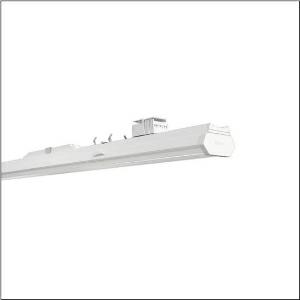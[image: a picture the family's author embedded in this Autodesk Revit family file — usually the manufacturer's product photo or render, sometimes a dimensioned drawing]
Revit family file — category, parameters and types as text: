
# Revit family: licross_r__11_protected_mo_51ts12vn465fd_14fd
name_source: partatom
category: Lighting Fixtures
units: mm (PartAtom-declared; Revit-internal decimal feet)

## family parameters
Cut with Voids When Loaded = No
Host = Face
Light Source = No
Part Type = Normal
Room Calculation Point = No
Round Connector Dimension = Use Diameter
Shared = No

## types (1)
- --- (1 x LED, 1000 lm, 8 W, 4000K)
    Apparent Load = 8 VA
    CIE Flux Codes = 54 82 95 97 100
    Color Rendering = 80
    Color Temperature = 4000K
    Default Elevation = 1800 mm
    Description = Licross® 11 Protected MO, luminaire insert, of sheet steel, galvanised, coil coated, white, length: 1.500mm, width: 90mm, height: 101mm, LED rated luminous flux: 6.530lm, light colour: 840, control gear: DALI 2, CLO, control gear: ECG DALI, with plug, 6-pole, with phase selection, mains connection: 220..240V, AC/DC, 0/50..60Hz, halogen-free wiring, for central battery installations according to DIN EN 60598-2-22, for emergency light function, without changeover relay, primary optical cover: cover, of PMMA, light emission: direct with ceiling illumination distribution, protection rating (complete): IP50, insulation class (complete): insulation class I (protective earthing), certification: CE, ENEC, VDE, UKCA, protection symbol: D if used in an environment with non-conductive dust loads with corresponding accessories, permissible ambient temperature for indoor applications: -25..+40°C, standard: EN 60598-2-22, corresponds to IFS (International Featured Standards) requirements for safety and quality in the food industry, reducing of maximum allowable ambient temperature of 5°C with ceiling mounting, packaging unit: 1 piece
    Height = 92 mm
    Lamp = 1 x LED
    Lamp Light Flux = 1000 lm
    Lamp Power = 8 W
    Lamp count = 1
    Length = 1500 mm
    Luminous efficacy = 125 lm/W
    Manufacturer = Siteco
    ModVariant = No
    Model = 51TS12VN465FD
    Mounting Place = Ceiling
    Mounting Type = Pendant
    Number of Poles = 1
    OnlyDefault = Yes
    Power Factor = 1
    Product Name = Licross® 11 Protected MO
    Product group = luminaire insert
    ProductGroupID = 902
    Protection Class = Protection class I
    Protection Degree = IP 50
    RLX_Detail_Level = 1
    RlxData = <blob elided: 24681 chars, md5=3b208eb1>
    Socket = socket
    Standby Power = 0 W
    System Light Flux = 1000 lm
    System Power = 8 W
    Type Comments = : DC mode (central or group accumulator) initial emergency light level
    Type Image = l_1256145.jpg
    URL = http://relux.com
    VarID = @adj_128621
    Voltage = 0 V
    Weight = 0.00 kg
    Width = 88 mm

## geometry (parser evidence)
native form markers: Blend x4, Sweep x10
no freeform markers — native parametric forms only
